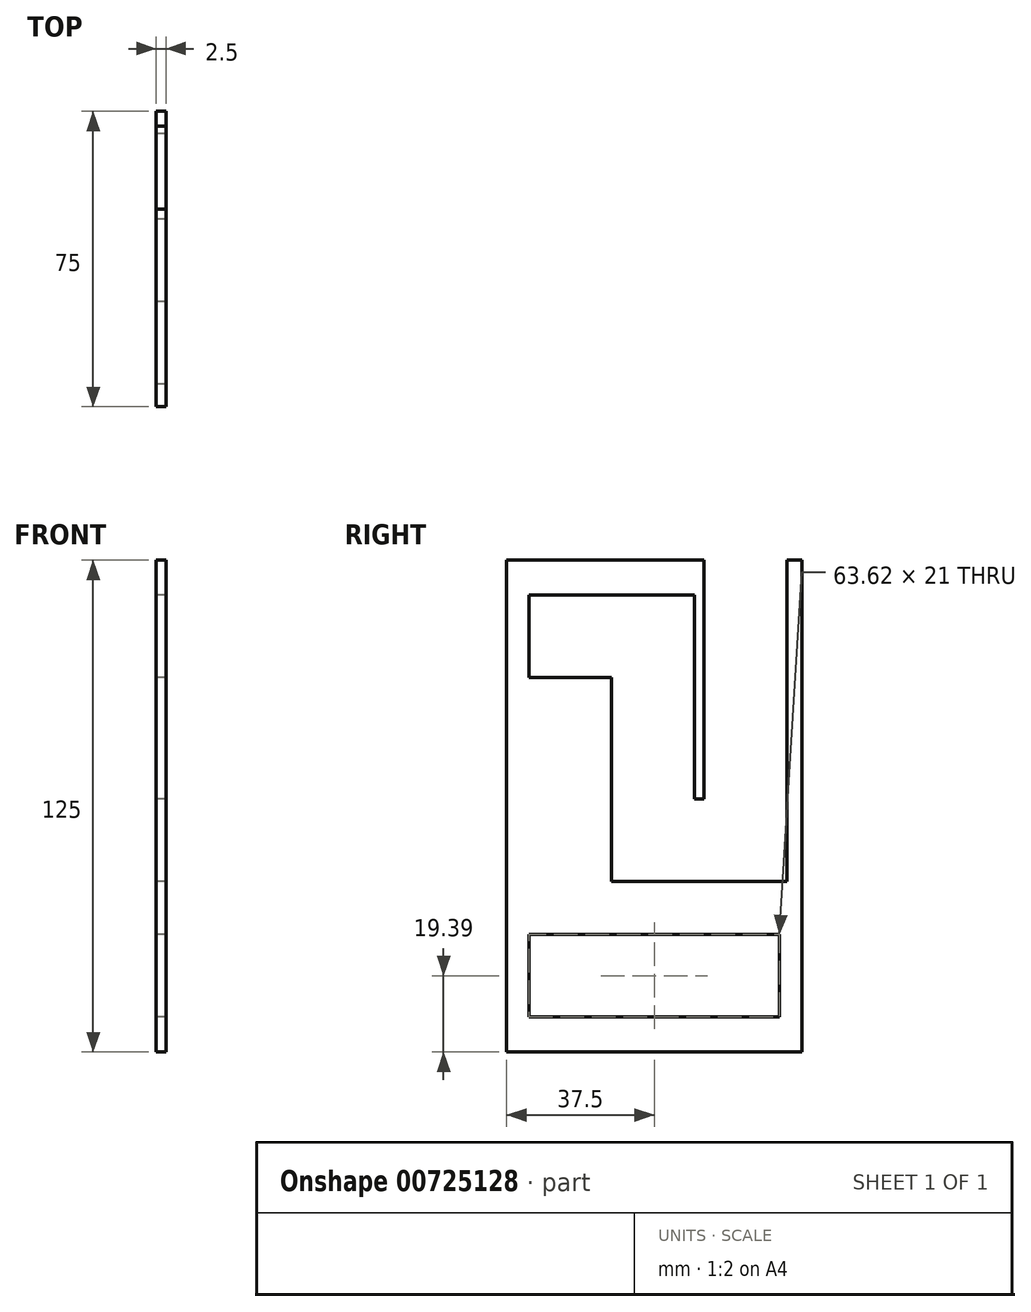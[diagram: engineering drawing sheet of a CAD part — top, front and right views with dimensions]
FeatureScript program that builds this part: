
annotation { "Feature Type Name" : "Feature", "Feature Type Description" : "" }
export const myFeature = defineFeature(function(context is Context, id is Id, definition is map)
    precondition{}
    {
        {
            var Q0;
            Q0=qCreatedBy(makeId("Right.planeOp"),FACE);
            var sketch = newSketch(context, id + "F0", { "sketchPlane" : qUnion([Q0])});
            skLineSegment(sketch, "E0.bottom", {"start": v(0, 0) * mm, "end": v(75, 0) * mm});
            skLineSegment(sketch, "E0.left", {"start": v(0, 0) * mm, "end": v(0, 125) * mm});
            skLineSegment(sketch, "E1.top", {"start": v(3.8, 3.81) * mm, "end": v(71.19, 3.81) * mm});
            skLineSegment(sketch, "E1.left", {"start": v(3.8, 121.19) * mm, "end": v(3.81, 3.8) * mm});
            skLineSegment(sketch, "E2.bottom", {"start": v(0, 125) * mm, "end": v(44.5, 125) * mm});
            skLineSegment(sketch, "E2.top", {"start": v(0, 125) * mm, "end": v(44.5, 125) * mm});
            skLineSegment(sketch, "E2.left", {"start": v(0, 125) * mm, "end": v(0, 125) * mm});
            skLineSegment(sketch, "E2.right", {"start": v(44.5, 125) * mm, "end": v(44.5, 125) * mm});
            skLineSegment(sketch, "E3", {"start": v(3.8, 121.19) * mm, "end": v(44.5, 121.19) * mm});
            skLineSegment(sketch, "E4", {"start": v(50.19, 121.2) * mm, "end": v(50.19, 125) * mm});
            skLineSegment(sketch, "E5", {"start": v(44.5, 125) * mm, "end": v(50.19, 125) * mm});
            skLineSegment(sketch, "E6", {"start": v(50.19, 121.19) * mm, "end": v(44.5, 121.19) * mm});
            skLineSegment(sketch, "E7", {"start": v(50.19, 121.2) * mm, "end": v(50.19, 64.36) * mm});
            skLineSegment(sketch, "E8", {"start": v(5.7, 8.89) * mm, "end": v(5.7, 29.89) * mm});
            skLineSegment(sketch, "E9", {"start": v(5.7, 29.89) * mm, "end": v(69.3, 29.9) * mm});
            skLineSegment(sketch, "E10", {"start": v(69.3, 29.9) * mm, "end": v(69.3, 8.9) * mm});
            skLineSegment(sketch, "E11", {"start": v(69.3, 8.9) * mm, "end": v(5.7, 8.89) * mm});
            skLineSegment(sketch, "E12", {"start": v(71.19, 3.81) * mm, "end": v(71.19, 125) * mm});
            skLineSegment(sketch, "E13", {"start": v(71.19, 125) * mm, "end": v(75, 125) * mm});
            skLineSegment(sketch, "E14", {"start": v(75, 125) * mm, "end": v(75, 0) * mm});
            skLineSegment(sketch, "E15", {"start": v(50.19, 64.36) * mm, "end": v(47.69, 64.36) * mm});
            skLineSegment(sketch, "E16", {"start": v(47.69, 64.36) * mm, "end": v(47.69, 121.2) * mm});
            skLineSegment(sketch, "E17", {"start": v(26.69, 95.11) * mm, "end": v(5.69, 95.11) * mm});
            skLineSegment(sketch, "E18", {"start": v(5.69, 95.11) * mm, "end": v(5.69, 116.11) * mm});
            skLineSegment(sketch, "E19", {"start": v(5.69, 116.11) * mm, "end": v(47.69, 116.11) * mm});
            skLineSegment(sketch, "E20", {"start": v(26.69, 95.11) * mm, "end": v(26.69, 43.36) * mm});
            skLineSegment(sketch, "E21", {"start": v(26.69, 43.36) * mm, "end": v(71.19, 43.36) * mm});
            skSolve(sketch);
        }
        {
            var Q0;
            Q0 = qSketchRegion(id + "F0", true);
            extrude(context, id + "F1", {"entities" : qUnion([Q0]), "depth" : 2.5 * mm, "offsetDistance" : 25.4 * mm});
        }
    });
